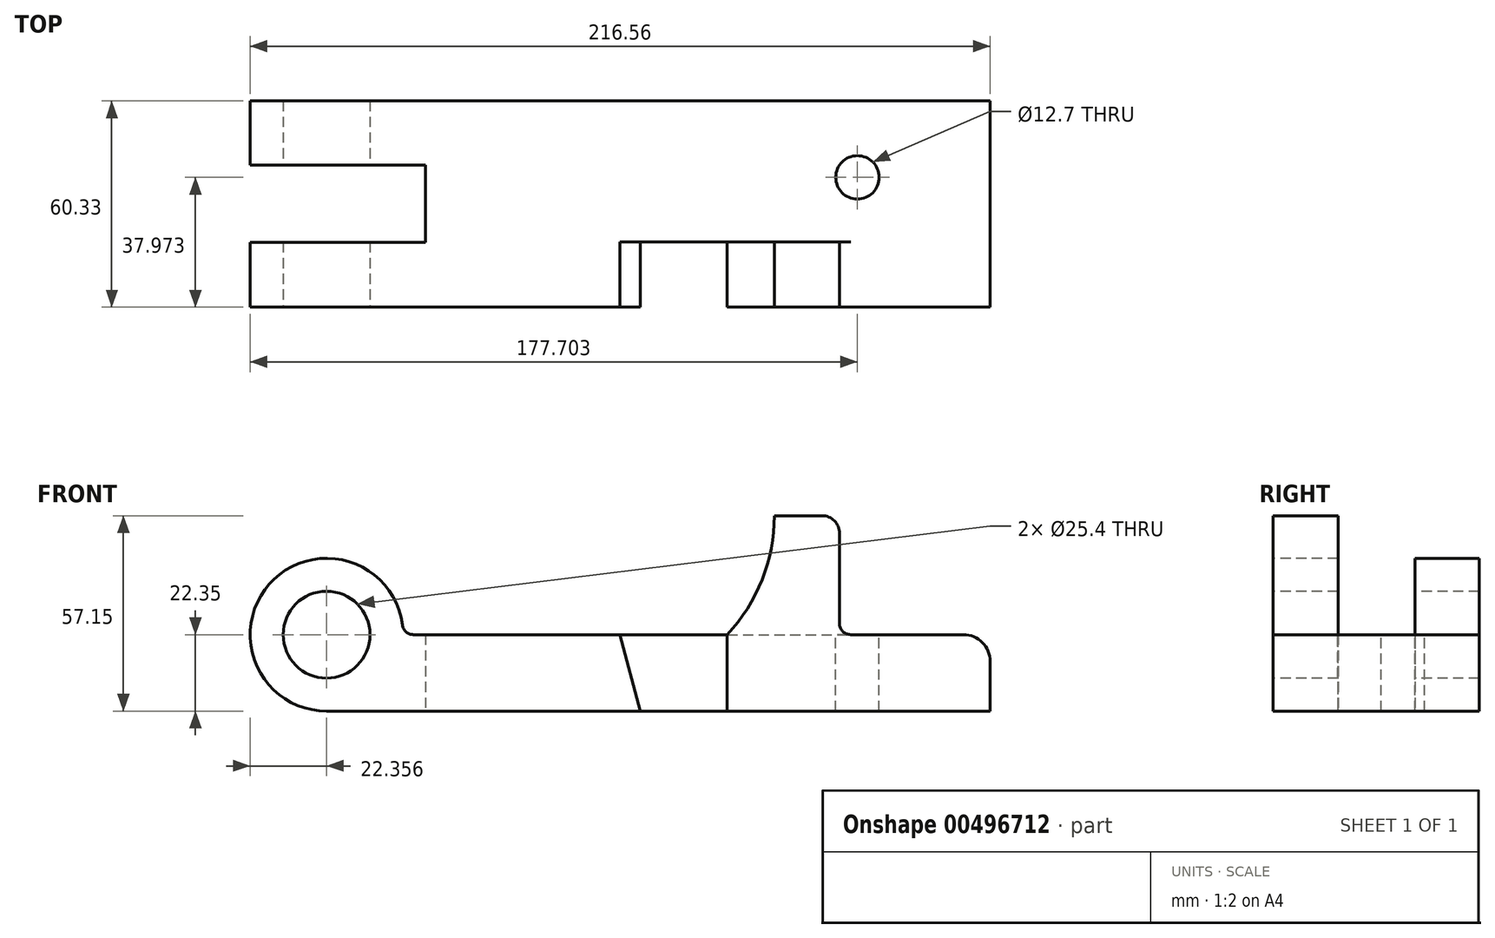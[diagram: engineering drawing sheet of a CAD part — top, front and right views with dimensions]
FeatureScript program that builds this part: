
annotation { "Feature Type Name" : "Feature", "Feature Type Description" : "" }
export const myFeature = defineFeature(function(context is Context, id is Id, definition is map)
    precondition{}
    {
        {
            var Q0;
            Q0=qCreatedBy(makeId("Front.planeOp"),FACE);
            var sketch = newSketch(context, id + "F0", { "sketchPlane" : qUnion([Q0])});
            skCircle(sketch, "E0", {"center": v(-72.56, 0) * mm, "radius": 12.7 * mm});
            skArc(sketch, "E1", {"start": v(-50.4, 2.88) * mm, "mid": v(-89.36, 14.75) * mm, "end": v(-72.56, -22.35) * mm});
            skLineSegment(sketch, "E2", {"start": v(-47.12, 0) * mm, "end": v(44.68, 0) * mm});
            skLineSegment(sketch, "E3", {"start": v(44.68, 0) * mm, "end": v(44.68, -22.35) * mm});
            skLineSegment(sketch, "E4", {"start": v(44.68, -22.35) * mm, "end": v(-72.56, -22.35) * mm});
            skLineSegment(sketch, "E5", {"start": v(13.29, 0) * mm, "end": v(19.28, -22.35) * mm});
            skLineSegment(sketch, "E6", {"start": v(44, 0.02) * mm, "end": v(44.68, 0) * mm});
            skLineSegment(sketch, "E7", {"start": v(44.68, -22.35) * mm, "end": v(121.64, -22.35) * mm});
            skLineSegment(sketch, "E8", {"start": v(121.64, -22.35) * mm, "end": v(121.64, -7.87) * mm});
            skLineSegment(sketch, "E9", {"start": v(113.77, 0) * mm, "end": v(80.83, 0) * mm});
            skPoint(sketch, "E10.visualSharp", {"position": v(121.64, 0) * mm});
            skLineSegment(sketch, "E10.filletArc", {"start": v(121.64, 0) * mm, "end": v(121.64, 0) * mm});
            skArc(sketch, "E11.filletArc", {"start": v(121.64, -7.87) * mm, "mid": v(119.34, -2.3) * mm, "end": v(113.77, 0) * mm});
            skLineSegment(sketch, "E12", {"start": v(44.68, 0) * mm, "end": v(44.68, 0) * mm});
            skLineSegment(sketch, "E13", {"start": v(58.48, 34.8) * mm, "end": v(72.45, 34.8) * mm});
            skLineSegment(sketch, "E14", {"start": v(77.53, 29.72) * mm, "end": v(77.53, 3.3) * mm});
            skPoint(sketch, "E15.visualSharp", {"position": v(77.53, 0) * mm});
            skArc(sketch, "E15.filletArc", {"start": v(77.53, 3.3) * mm, "mid": v(78.5, 0.97) * mm, "end": v(80.83, 0) * mm});
            skPoint(sketch, "E16.visualSharp", {"position": v(-50.21, 0) * mm});
            skArc(sketch, "E16.filletArc", {"start": v(-50.4, 2.88) * mm, "mid": v(-49.3, 0.82) * mm, "end": v(-47.12, 0) * mm});
            skArc(sketch, "E17", {"start": v(44.68, 0) * mm, "mid": v(54.9, 16.08) * mm, "end": v(58.48, 34.8) * mm});
            skPoint(sketch, "E18.visualSharp", {"position": v(77.53, 34.8) * mm});
            skArc(sketch, "E18.filletArc", {"start": v(77.53, 29.72) * mm, "mid": v(76.04, 33.31) * mm, "end": v(72.45, 34.8) * mm});
            skLineSegment(sketch, "E19", {"start": v(44.68, 0) * mm, "end": v(80.83, 0) * mm});
            skSolve(sketch);
        }
        {
            var Q0;
            Q0=makeQuery(id+"F0.imprint","IMPRINT",FACE,{"disambiguationData":[TD([[makeQuery(id+"F0.imprint","IMPRINT",EDGE,{"derivedFrom":sQuery(id+"F0.wireOp",EDGE,"E0")}),-1.0]])]});
            var Q1;
            {var subQ0=sQuery(id+"F0.wireOp",EDGE,"E3");Q1=makeQuery(id+"F0.imprint","IMPRINT",FACE,{"disambiguationData":[TD([[makeQuery(id+"F0.imprint","IMPRINT",EDGE,{"derivedFrom":subQ0}),-1.0]])]});}
            var Q2;
            Q2=makeQuery(id+"F0.imprint","IMPRINT",FACE,{"disambiguationData":[TD([[makeQuery(id+"F0.imprint","IMPRINT",EDGE,{"derivedFrom":sQuery(id+"F0.wireOp",EDGE,"E3")}),1.0]])]});
            extrude(context, id + "F1", {"entities" : qUnion([Q0, Q1, Q2]), "oppositeDirection" : true, "depth" : 60.32 * mm});
        }
        {
            var Q0;
            Q0=qCreatedBy(makeId("Top.planeOp"),FACE);
            var sketch = newSketch(context, id + "F2", { "sketchPlane" : qUnion([Q0])});
            skLineSegment(sketch, "E20", {"start": v(-94.92, 41.6) * mm, "end": v(-43.6, 41.6) * mm});
            skLineSegment(sketch, "E21", {"start": v(-43.6, 41.6) * mm, "end": v(-43.6, 19) * mm});
            skLineSegment(sketch, "E22", {"start": v(-43.6, 19) * mm, "end": v(-94.92, 19) * mm});
            skLineSegment(sketch, "E23", {"start": v(-94.92, 41.6) * mm, "end": v(-94.92, 19) * mm});
            skSolve(sketch);
        }
        {
            var Q0;
            Q0 = qSketchRegion(id + "F2", true);
            extrude(context, id + "F3", {"entities" : qUnion([Q0]), "operationType" : NewBodyOperationType.REMOVE, "depth" : 111.76 * mm, "symmetric" : true});
        }
        {
            var Q0;
            {var subQ0=sQuery(id+"F0.wireOp",EDGE,"E3");Q0=makeQuery(id+"F0.imprint","IMPRINT",FACE,{"disambiguationData":[TD([[makeQuery(id+"F0.imprint","IMPRINT",EDGE,{"derivedFrom":subQ0}),-1.0]])]});}
            extrude(context, id + "F4", {"entities" : qUnion([Q0]), "operationType" : NewBodyOperationType.REMOVE, "oppositeDirection" : true, "depth" : 19.05 * mm});
        }
        {
            var Q0;
            Q0=makeQuery(id+"F0.imprint","IMPRINT",FACE,{"disambiguationData":[TD([[makeQuery(id+"F0.imprint","IMPRINT",EDGE,{"derivedFrom":sQuery(id+"F0.wireOp",EDGE,"E13")}),-1.0]])]});
            extrude(context, id + "F5", {"entities" : qUnion([Q0]), "operationType" : NewBodyOperationType.ADD, "oppositeDirection" : true, "depth" : 19.05 * mm});
        }
        {
            var Q0;
            Q0=qCreatedBy(makeId("Top.planeOp"),FACE);
            var sketch = newSketch(context, id + "F6", { "sketchPlane" : qUnion([Q0])});
            skCircle(sketch, "E24", {"center": v(82.78, 37.97) * mm, "radius": 6.35 * mm});
            skPoint(sketch, "E25.0.start.orphan", {"position": v(-47.12, 60.33) * mm});
            skPoint(sketch, "E26.0.end.orphan", {"position": v(121.64, 0) * mm});
            skSolve(sketch);
        }
        {
            var Q0;
            Q0=makeQuery(id+"F6.imprint","IMPRINT",FACE,{"disambiguationData":[TD([[makeQuery(id+"F6.imprint","IMPRINT",EDGE,{"derivedFrom":sQuery(id+"F6.wireOp",EDGE,"E24")}),1.0]])]});
            extrude(context, id + "F7", {"entities" : qUnion([Q0]), "operationType" : NewBodyOperationType.REMOVE, "endBound" : BoundingType.THROUGH_ALL, "oppositeDirection" : true, "depth" : 25.4 * mm});
        }
    });
